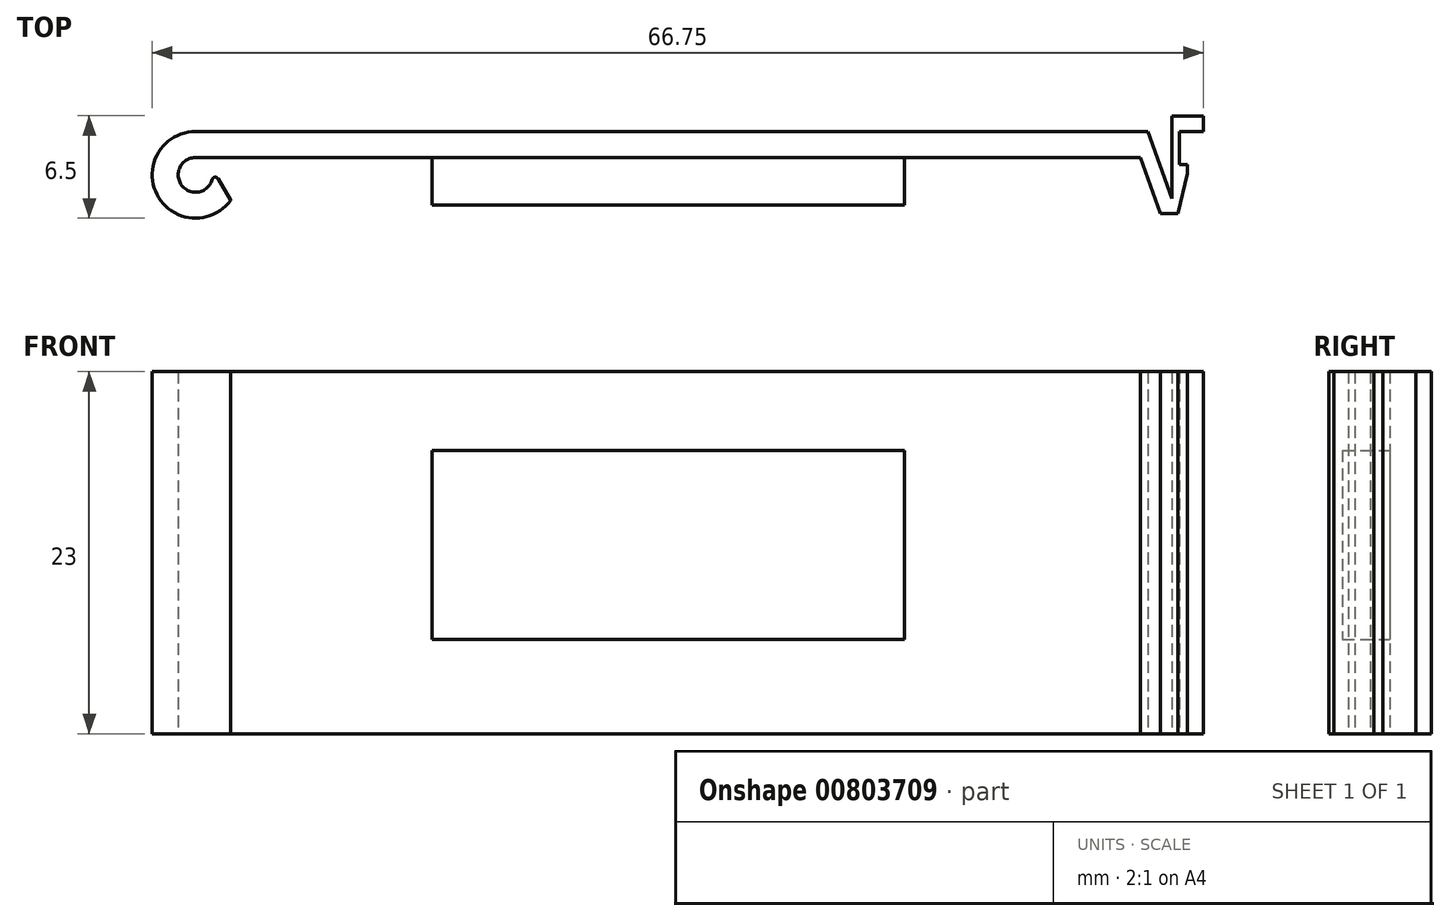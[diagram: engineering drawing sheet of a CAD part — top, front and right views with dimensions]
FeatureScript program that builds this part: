
annotation { "Feature Type Name" : "Feature", "Feature Type Description" : "" }
export const myFeature = defineFeature(function(context is Context, id is Id, definition is map)
    precondition{}
    {
        {
            var Q0;
            Q0=qCreatedBy(makeId("Top.planeOp"),FACE);
            var sketch = newSketch(context, id + "F0", { "sketchPlane" : qUnion([Q0])});
            skLineSegment(sketch, "E0", {"start": v(-41.77, -46.22) * mm, "end": v(-101.8, -46.22) * mm});
            skArc(sketch, "E1", {"start": v(-101.8, -46.22) * mm, "mid": v(-102.67, -48) * mm, "end": v(-100.73, -47.62) * mm});
            skLineSegment(sketch, "E2", {"start": v(-99.57, -48.91) * mm, "end": v(-100.37, -47.57) * mm});
            skArc(sketch, "E3", {"start": v(-101.8, -44.57) * mm, "mid": v(-104.24, -48.57) * mm, "end": v(-99.57, -48.94) * mm});
            skLineSegment(sketch, "E4", {"start": v(-41.77, -46.22) * mm, "end": v(-40.52, -49.77) * mm});
            skLineSegment(sketch, "E5", {"start": v(-101.8, -44.57) * mm, "end": v(-41.3, -44.57) * mm});
            skLineSegment(sketch, "E6", {"start": v(-41.3, -44.57) * mm, "end": v(-39.8, -48.84) * mm});
            skLineSegment(sketch, "E7", {"start": v(-39.8, -48.84) * mm, "end": v(-39.8, -43.57) * mm});
            skLineSegment(sketch, "E8", {"start": v(-39.8, -43.57) * mm, "end": v(-37.8, -43.57) * mm});
            skLineSegment(sketch, "E9", {"start": v(-37.8, -43.57) * mm, "end": v(-37.8, -44.57) * mm});
            skLineSegment(sketch, "E10", {"start": v(-37.8, -44.57) * mm, "end": v(-38.8, -44.57) * mm});
            skLineSegment(sketch, "E11", {"start": v(-38.8, -46.67) * mm, "end": v(-38.8, -49.77) * mm});
            skPoint(sketch, "E12.visualSharp", {"position": v(-38.8, -54.7) * mm});
            skLineSegment(sketch, "E13", {"start": v(-38.8, -46.67) * mm, "end": v(-39.3, -46.67) * mm});
            skLineSegment(sketch, "E14", {"start": v(-39.3, -46.67) * mm, "end": v(-39.3, -44.57) * mm});
            skLineSegment(sketch, "E15", {"start": v(-39.3, -44.57) * mm, "end": v(-38.8, -44.57) * mm});
            skPoint(sketch, "E16.visualSharp", {"position": v(-97, -53.23) * mm});
            skPoint(sketch, "E17.visualSharp", {"position": v(-100.85, -46.76) * mm});
            skArc(sketch, "E17.filletArc", {"start": v(-100.37, -47.57) * mm, "mid": v(-100.57, -47.47) * mm, "end": v(-100.73, -47.62) * mm});
            skLineSegment(sketch, "E18", {"start": v(-38.8, -49.77) * mm, "end": v(-40.52, -49.77) * mm});
            skPoint(sketch, "E19.visualSharp", {"position": v(-99.46, -49.08) * mm});
            skPoint(sketch, "E20.visualSharp", {"position": v(-99.56, -48.93) * mm});
            skArc(sketch, "E20.filletArc", {"start": v(-99.57, -48.94) * mm, "mid": v(-99.56, -48.93) * mm, "end": v(-99.57, -48.91) * mm});
            skSolve(sketch);
        }
        {
            var Q0;
            Q0 = qSketchRegion(id + "F0", true);
            extrude(context, id + "F1", {"entities" : qUnion([Q0]), "depth" : 23 * mm, "offsetDistance" : 25 * mm});
        }
        {
            var Q0;
            Q0=makeQuery(id+"F1.opExtrude","CAP_FACE",FACE,{"disambiguationData":[OSD([sQuery(id+"F0.wireOp",EDGE,"E0"),sQuery(id+"F0.wireOp",EDGE,"E1"),sQuery(id+"F0.wireOp",EDGE,"E2"),sQuery(id+"F0.wireOp",EDGE,"E3"),sQuery(id+"F0.wireOp",EDGE,"E4"),sQuery(id+"F0.wireOp",EDGE,"E5"),sQuery(id+"F0.wireOp",EDGE,"E6"),sQuery(id+"F0.wireOp",EDGE,"E7"),sQuery(id+"F0.wireOp",EDGE,"E8"),sQuery(id+"F0.wireOp",EDGE,"E9"),sQuery(id+"F0.wireOp",EDGE,"E10"),sQuery(id+"F0.wireOp",EDGE,"E11"),sQuery(id+"F0.wireOp",EDGE,"E13"),sQuery(id+"F0.wireOp",EDGE,"E14"),sQuery(id+"F0.wireOp",EDGE,"E15"),sQuery(id+"F0.wireOp",EDGE,"E17.filletArc"),sQuery(id+"F0.wireOp",EDGE,"E18"),sQuery(id+"F0.wireOp",EDGE,"c3kMcTmM-fs2w-JIPq-A91t-aECWDBtJ1je9"),sQuery(id+"F0.wireOp",EDGE,"E19.filletArc")])],"isStart":true});
            var sketch = newSketch(context, id + "F2", { "sketchPlane" : qUnion([Q0])});
            skLineSegment(sketch, "E21", {"start": v(-38.8, 47.24) * mm, "end": v(-39.39, 49.77) * mm});
            skLineSegment(sketch, "E22", {"start": v(-39.39, 49.77) * mm, "end": v(-38.8, 49.77) * mm});
            skLineSegment(sketch, "E23", {"start": v(-38.8, 49.77) * mm, "end": v(-38.8, 47.24) * mm});
            skSolve(sketch);
        }
        {
            var Q0;
            Q0 = qSketchRegion(id + "F2", true);
            extrude(context, id + "F3", {"entities" : qUnion([Q0]), "operationType" : NewBodyOperationType.REMOVE, "oppositeDirection" : true, "depth" : 25 * mm, "offsetDistance" : 25 * mm});
        }
        {
            var Q0;
            Q0=makeQuery(id+"F1.opExtrude","SWEPT_FACE",FACE,{"disambiguationData":[OSD([sQuery(id+"F0.wireOp",EDGE,"E0")])]});
            var sketch = newSketch(context, id + "F4", { "sketchPlane" : qUnion([Q0])});
            skLineSegment(sketch, "E24.bottom", {"start": v(-86.77, 18) * mm, "end": v(-56.77, 18) * mm});
            skLineSegment(sketch, "E24.top", {"start": v(-86.77, 6) * mm, "end": v(-56.77, 6) * mm});
            skLineSegment(sketch, "E24.left", {"start": v(-86.77, 18) * mm, "end": v(-86.77, 6) * mm});
            skLineSegment(sketch, "E24.right", {"start": v(-56.77, 18) * mm, "end": v(-56.77, 6) * mm});
            skSolve(sketch);
        }
        {
            var Q0;
            Q0 = qSketchRegion(id + "F4", true);
            extrude(context, id + "F5", {"entities" : qUnion([Q0]), "operationType" : NewBodyOperationType.ADD, "depth" : 3 * mm, "offsetDistance" : 25 * mm});
        }
    });
